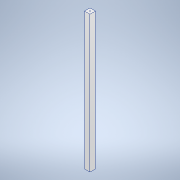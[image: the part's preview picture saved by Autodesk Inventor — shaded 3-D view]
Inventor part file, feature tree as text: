
AUTODESK INVENTOR PART (.ipt)
format: ipt  version: 2020 (Build 240168000, 168)  size: 107,008 bytes
history: native  units: mm
features: sketch x2, other x1, extrude x1, hole x1
ambient origin geometry x8: Origin, YZ Plane, XZ Plane, XY Plane, X Axis, Y Axis, Z Axis, Center Point
bodies: Solid1 (feature_tree)
feature tree (5):
  other  "<userpath>\Documents\Development\paragon-printer\Paragon Printer Parameters.xlsx"
  extrude  "Extrusion1"  Depth=20.0mm
  hole  "Hole1"  [1 undecoded]
  sketch  "Sketch1"  dims[d0=20.0mm d1=20.0mm]
  sketch  "Sketch2"  dims[d2=500.0mm d3=0.0mm d4=3.4mm d5=6.0mm d6=6.3mm d7=2.0mm d8=90.0deg d9=8.0mm d10=20.594885mm]
note: 1 required parameter value undecoded (feature->parameter linkage not recoverable at this tier; creation-order binding heuristic only, values carry confidence <= 0.55)
